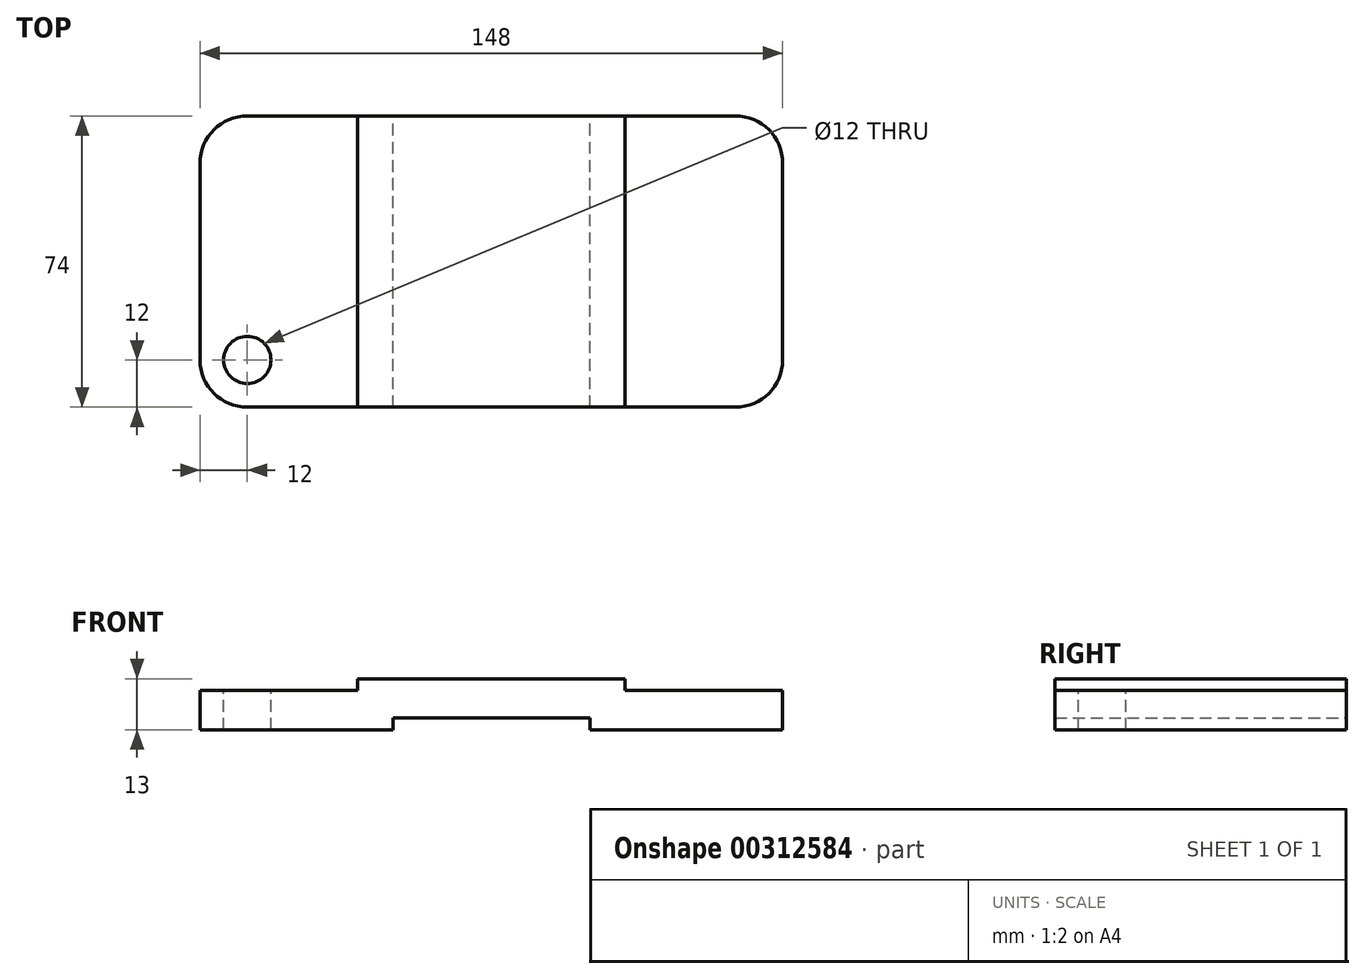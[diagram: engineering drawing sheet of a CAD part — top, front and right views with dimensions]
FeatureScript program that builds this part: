
annotation { "Feature Type Name" : "Feature", "Feature Type Description" : "" }
export const myFeature = defineFeature(function(context is Context, id is Id, definition is map)
    precondition{}
    {
        {
            var Q0;
            Q0=qCreatedBy(makeId("Front.planeOp"),FACE);
            var sketch = newSketch(context, id + "F0", { "sketchPlane" : qUnion([Q0])});
            skLineSegment(sketch, "E0", {"start": v(0, 3) * mm, "end": v(-25, 3) * mm});
            skLineSegment(sketch, "E1", {"start": v(-25, 3) * mm, "end": v(-25, 0) * mm});
            skLineSegment(sketch, "E2", {"start": v(-25, 0) * mm, "end": v(-74, 0) * mm});
            skLineSegment(sketch, "E3", {"start": v(-74, 0) * mm, "end": v(-74, 10) * mm});
            skLineSegment(sketch, "E4", {"start": v(-74, 10) * mm, "end": v(-34, 10) * mm});
            skLineSegment(sketch, "E5", {"start": v(-34, 10) * mm, "end": v(-34, 13) * mm});
            skLineSegment(sketch, "E6", {"start": v(-34, 13) * mm, "end": v(0, 13) * mm});
            skLineSegment(sketch, "E7", {"start": v(0, 36.6) * mm, "end": v(0, -22.94) * mm, "construction": true});
            skLineSegment(sketch, "E8.MirrorCS", {"start": v(25, 3) * mm, "end": v(25, 0) * mm});
            skLineSegment(sketch, "E9.MirrorCS", {"start": v(34, 10) * mm, "end": v(34, 13) * mm});
            skLineSegment(sketch, "E10.MirrorCS", {"start": v(25, 0) * mm, "end": v(74, 0) * mm});
            skLineSegment(sketch, "E11.MirrorCS", {"start": v(74, 10) * mm, "end": v(34, 10) * mm});
            skLineSegment(sketch, "E12.MirrorCS", {"start": v(74, 0) * mm, "end": v(74, 10) * mm});
            skLineSegment(sketch, "E13.MirrorCS", {"start": v(34, 13) * mm, "end": v(0, 13) * mm});
            skLineSegment(sketch, "E14.MirrorCS", {"start": v(0, 3) * mm, "end": v(25, 3) * mm});
            skSolve(sketch);
        }
        {
            var Q0;
            Q0=makeQuery(id+"F0.imprint","IMPRINT",FACE,{"disambiguationData":[TD([[makeQuery(id+"F0.imprint","IMPRINT",EDGE,{"derivedFrom":sQuery(id+"F0.wireOp",EDGE,"E0")}),-1.0]])]});
            extrude(context, id + "F1", {"entities" : qUnion([Q0]), "endBound" : BoundingType.SYMMETRIC, "depth" : 74 * mm});
        }
        {
            var Q0;
            Q0=makeQuery(id+"F1.opExtrude","CAP_EDGE",EDGE,{"disambiguationData":[OSD([sQuery(id+"F0.wireOp",EDGE,"E12.MirrorCS")])],"isStart":false});
            var Q1;
            Q1=makeQuery(id+"F1.opExtrude","CAP_EDGE",EDGE,{"disambiguationData":[OSD([sQuery(id+"F0.wireOp",EDGE,"E12.MirrorCS")])],"isStart":true});
            var Q2;
            Q2=makeQuery(id+"F1.opExtrude","CAP_EDGE",EDGE,{"disambiguationData":[OSD([sQuery(id+"F0.wireOp",EDGE,"E3")])],"isStart":false});
            var Q3;
            Q3=makeQuery(id+"F1.opExtrude","CAP_EDGE",EDGE,{"disambiguationData":[OSD([sQuery(id+"F0.wireOp",EDGE,"E3")])],"isStart":true});
            fillet(context, id + "F2", {"entities" : qUnion([Q0, Q1, Q2, Q3]), "radius" : 12 * mm, "tangentPropagation" : true, "allowEdgeOverflow" : false});
        }
        {
            var Q0;
            Q0=makeQuery(id+"F1.opExtrude","SWEPT_FACE",FACE,{"disambiguationData":[OSD([sQuery(id+"F0.wireOp",EDGE,"E4")])]});
            var sketch = newSketch(context, id + "F3", { "sketchPlane" : qUnion([Q0])});
            skCircle(sketch, "E15", {"center": v(-62, -25) * mm, "radius": 6 * mm});
            skSolve(sketch);
        }
        {
            var Q0;
            Q0=makeQuery(id+"F3.imprint","IMPRINT",FACE,{"disambiguationData":[TD([[makeQuery(id+"F3.imprint","IMPRINT",EDGE,{"derivedFrom":sQuery(id+"F3.wireOp",EDGE,"E15")}),1.0]])]});
            extrude(context, id + "F4", {"entities" : qUnion([Q0]), "operationType" : NewBodyOperationType.REMOVE, "oppositeDirection" : true, "depth" : 25 * mm});
        }
    });
